# Revit family: Gewindeplatte Vierkant
name_source: partatom
category: HLS-Bauteile
revit_build: Autodesk Revit 2017 (Build: 20190507_1515(x64)
units: mm (PartAtom-declared; Revit-internal decimal feet)

## family parameters
Arbeitsebenenbasiert = Ja
Beim Laden mit Abzugskörper schneiden = Nein
Bemaßung runder Anschluss = Durchmesser verwenden
Gemeinsam genutzt = Ja
Immer vertikal = Nein
Raumberechnungspunkt = Nein
Teiletyp = Normal

## types (4) — shared parameters
Anzugsmoment = 0.00 kN-m
B = 30 mm  [stored 0.0984252 ft]
Breite = 30 mm  [stored 0.0984252 ft]
Fabrikat = MEFA
Firma = MEFA Befestigungs- und Montagesysteme GmbH
Form = vierkant
Kurztext1 = Gewindeplatte
L = 35 mm  [stored 0.114829 ft]
Länge = 35 mm  [stored 0.114829 ft]
Material = Stahl
Materialname = S235
Mengeneinheit = St
Oberflaeche = galvanisch verzinkt
Profil = C-Profil
Profiltyp = 35, 45
Schienenbreite = 35 mm
Vorgabe-Ansicht = 1219 mm
vpe = 50 St

## per-type parameters (varying)
| type | Abmessung | Artikelnummer | EAN | Gewicht | Gewicht pro Bauteil | Gewinde | Kurztext2 | S | Stärke Material | d2 |
| Gewindeplatte Vierkant 30x35x6 M 8 | 35 x 30 x 6 mm | 0816112 | 4250928420169 | 0.05 kg | 0.05 kg | M8 | M8 vierkant 35 x 30 mm gvz | 8 mm  [stored 0.0262467 ft] | 6 mm  [stored 0.019685 ft] | 3 mm  [stored 0.00984252 ft] |
| Gewindeplatte Vierkant 30x35x6 M10 | 35 x 30 x 6 mm | 081612001 | 4250928420176 | 0.05 kg | 0.05 kg | M10 | M10 vierkant 35 x 30 mm gvz | 6 mm  [stored 0.019685 ft] | 6 mm  [stored 0.019685 ft] | 4 mm  [stored 0.0131234 ft] |
| Gewindeplatte Vierkant 30x35x6 M12 | 35 x 30 x 6 mm | 081613801 | 4250928420183 | 0.05 kg | 0.05 kg | M12 | M12 vierkant 35 x 30 mm gvz | 6 mm  [stored 0.019685 ft] | 6 mm  [stored 0.019685 ft] | 5 mm  [stored 0.0164042 ft] |
| Gewindeplatte Vierkant 30x 35x8 M16 | 35 x 30 x 8 mm | 0816146 | 4250928420190 | 0.06 kg | 0.06 kg | M16 | M16 vierkant 35 x 30 mm gvz | 8 mm  [stored 0.0262467 ft] | 8 mm  [stored 0.0262467 ft] | 7 mm  [stored 0.0229659 ft] |

note: [stored X ft] marks values corroborated as IEEE doubles in the binary element streams (Revit-internal decimal feet)
